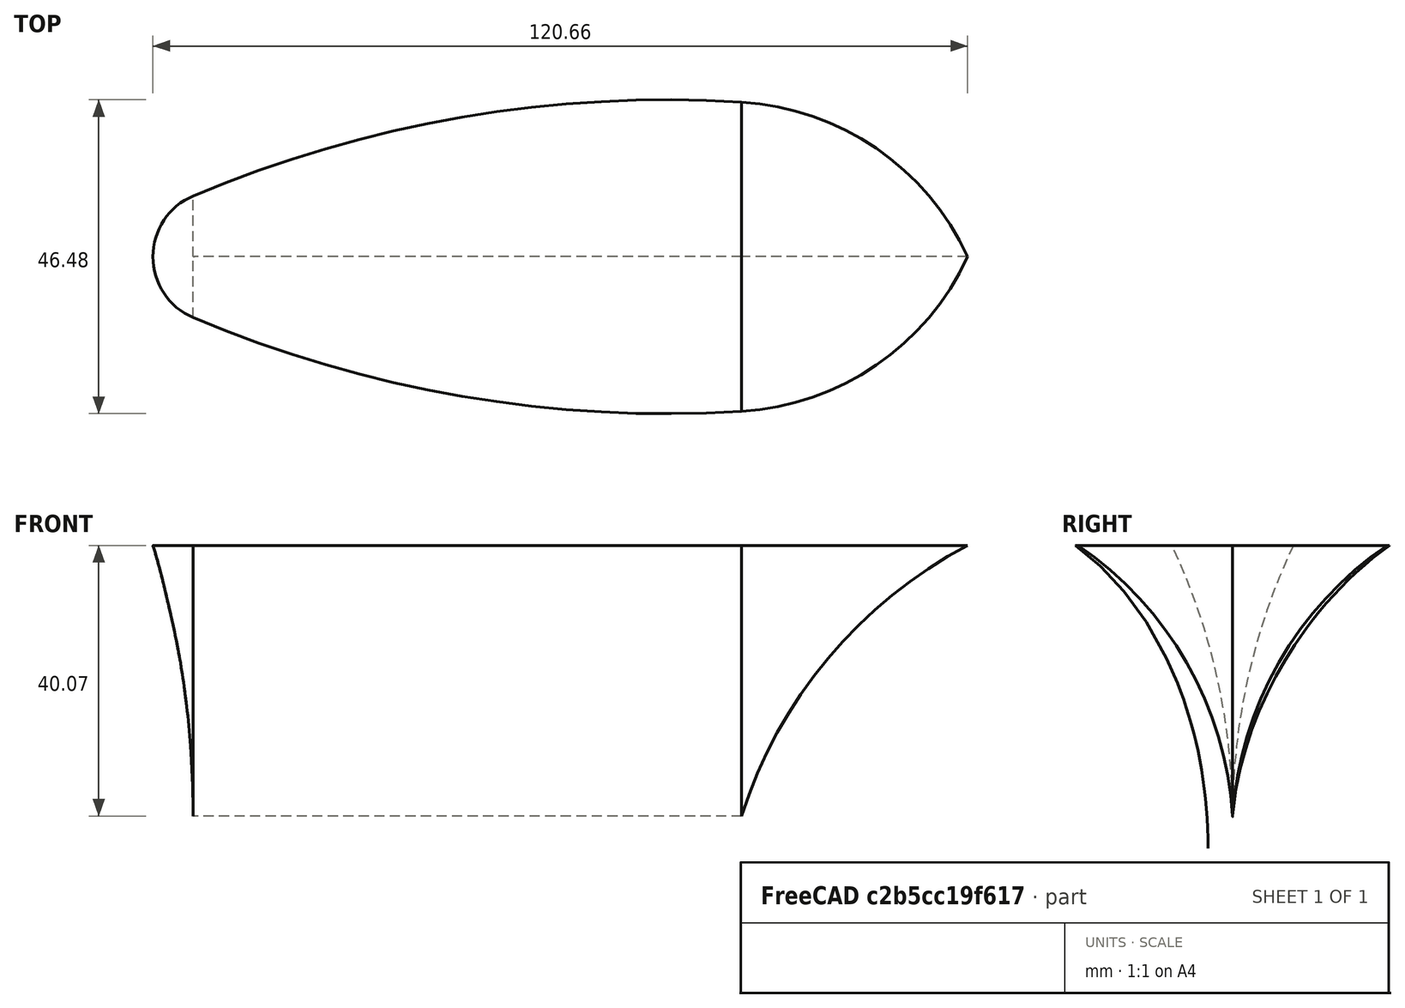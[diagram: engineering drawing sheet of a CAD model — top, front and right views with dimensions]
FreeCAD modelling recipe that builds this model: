
FCSTD DOCUMENT  (FreeCAD 0.21R33771 (Git))
Label: ship
License: All rights reserved
LicenseURL: http://en.wikipedia.org/wiki/All_rights_reserved
objects: Surface::Filling×6, Sketcher::SketchObject×5, Part::RuledSurface×1
note: 12 computed .brp shape members not serialized (recipe doc carries the construction recipe); baked Part::Feature solids carry a one-line shape summary decoded from their .brp

FEATURE [Sketcher::SketchObject] Sketch
  FullyConstrained = false
  sketch-geometry (7):
    g0: ArcOfCircle CenterX=-43.5861 CenterY=0 CenterZ=0 NormalX=0 NormalY=0 NormalZ=1 AngleXU=0 Radius=9.7712 StartAngle=1.97126 EndAngle=4.31193
    g1: ArcOfCircle CenterX=31.4054 CenterY=-16.5595 CenterZ=0 NormalX=0 NormalY=0 NormalZ=1 AngleXU=0 Radius=39.5318 StartAngle=0.432222 EndAngle=1.50927
    g2: ArcOfCircle CenterX=31.4054 CenterY=16.5595 CenterZ=0 NormalX=0 NormalY=0 NormalZ=1 AngleXU=0 Radius=39.5318 StartAngle=4.77392 EndAngle=5.85096
    g3: ArcOfCircle CenterX=22.7694 CenterY=-156.743 CenterZ=0 NormalX=0 NormalY=0 NormalZ=1 AngleXU=0 Radius=179.981 StartAngle=1.50927 EndAngle=1.97126
    g4: ArcOfCircle CenterX=22.7694 CenterY=156.743 CenterZ=0 NormalX=0 NormalY=0 NormalZ=1 AngleXU=0 Radius=179.981 StartAngle=4.31193 EndAngle=4.77392
    g5: LineSegment StartX=67.3018 StartY=-7.1e-15 StartZ=0 EndX=33.8361 EndY=0 EndZ=0
    g6: LineSegment StartX=-53.3573 StartY=0 StartZ=0 EndX=-47.3953 EndY=0 EndZ=0
  constraints (17):
    c: PointOnObject(g1,g-1)
    c: Coincident(g2,g1)
    c: Equal(g1,g2)
    c: Vertical(g1,g2)
    c: Tangent(g3,g0) = -1.5708
    c: Tangent(g4,g0) = -1.5708
    c: Tangent(g3,g1) = -1.5708
    c: Tangent(g4,g2) = -1.5708
    c: PointOnObject(g0,g-1)
    c: Vertical(g0,g0)
    c: Coincident(g5,g1)
    c: PointOnObject(g5,g-1)
    c: Vertical(g1,g5)
    c: PointOnObject(g6,g0)
    c: PointOnObject(g6,g-1)
    c: Horizontal(g6)
    c: Vertical(g0,g6)
FEATURE [Sketcher::SketchObject] Sketch001
  ExternalGeometry = -> [Sketch]
  FullyConstrained = false
  MapMode = 7
  Placement = pos=(33.8361,0,0) rot=(0.57735,0.57735,0.57735;2.0944rad)
  Support = -> [Sketch]
  sketch-geometry (2):
    g0: ArcOfCircle CenterX=-52.4068 CenterY=-43.4397 CenterZ=0 NormalX=0 NormalY=0 NormalZ=1 AngleXU=0 Radius=52.5148 StartAngle=0.0641414 EndAngle=0.974088
    g1: ArcOfCircle CenterX=52.4068 CenterY=-43.4397 CenterZ=0 NormalX=0 NormalY=0 NormalZ=1 AngleXU=0 Radius=52.5148 StartAngle=2.1675 EndAngle=3.07745
  constraints (4):
    c: Coincident(g0,g-4)
    c: Coincident(g1,g-3)
    c: Coincident(g1,g0)
    c: Symmetric(g0,g1,g-2)
FEATURE [Sketcher::SketchObject] Sketch002
  ExternalGeometry = -> [Sketch,Sketch001]
  FullyConstrained = false
  Placement = pos=(0,0,0) rot=(1,0,0;1.5708rad)
  sketch-geometry (2):
    g0: ArcOfCircle CenterX=99.3271 CenterY=-60.7549 CenterZ=0 NormalX=0 NormalY=0 NormalZ=1 AngleXU=0 Radius=68.6789 StartAngle=2.05591 EndAngle=2.83571
    g1: LineSegment StartX=33.8361 StartY=-40.0736 StartZ=0 EndX=-47.3953 EndY=-40.0736 EndZ=0
  constraints (5):
    c: Coincident(g0,g-3)
    c: Coincident(g0,g-4)
    c: Coincident(g1,g0)
    c: Horizontal(g1)
    c: Vertical(g-5,g1)
FEATURE [Sketcher::SketchObject] Sketch003
  ExternalGeometry = -> [Sketch002,Sketch]
  FullyConstrained = false
  MapMode = 7
  Placement = pos=(-47.3953,0,0) rot=(0.57735,-0.57735,-0.57735;2.0944rad)
  Support = -> [Sketch]
  sketch-geometry (2):
    g0: ArcOfCircle CenterX=93.7343 CenterY=-40.0736 CenterZ=0 NormalX=0 NormalY=0 NormalZ=1 AngleXU=0 Radius=93.7343 StartAngle=2.69984 EndAngle=3.14159
    g1: ArcOfCircle CenterX=-93.7344 CenterY=-40.0737 CenterZ=0 NormalX=0 NormalY=0 NormalZ=1 AngleXU=0 Radius=93.7344 StartAngle=3.42796e-07 EndAngle=0.441751
  constraints (4):
    c: Coincident(g0,g-3)
    c: Tangent(g0,g-2)
    c: Coincident(g1,g0)
    c: Tangent(g1,g-2)
FEATURE [Sketcher::SketchObject] Sketch004
  ExternalGeometry = -> [Sketch,Sketch003]
  FullyConstrained = true
  Placement = pos=(0,0,0) rot=(1,0,0;1.5708rad)
  sketch-geometry (1):
    g0: ArcOfCircle CenterX=-185.055 CenterY=-40.0736 CenterZ=0 NormalX=0 NormalY=0 NormalZ=1 AngleXU=0 Radius=137.66 StartAngle=6.28319 EndAngle=6.57857
  constraints (3):
    c: Coincident(g0,g-3)
    c: Coincident(g0,g-4)
    c: Tangent(g0,g-4)
FEATURE [Surface::Filling] Surface
  Anisotropy = false
  BoundaryEdges = -> [Sketch001,Sketch002,Sketch]
  BoundaryOrder = [0,0,0]
  Degree = 3
  Iterations = 2
  MaximumDegree = 8
  MaximumSegments = 9
  PointsOnCurve = 15
  TolAngular = 0.01
  TolCurvature = 0.1
  Tolerance2d = 1e-05
  Tolerance3d = 0.0001
FEATURE [Surface::Filling] Surface001
  Anisotropy = false
  BoundaryEdges = -> [Sketch002,Sketch001,Sketch]
  BoundaryOrder = [0,0,0]
  Degree = 3
  Iterations = 2
  MaximumDegree = 8
  MaximumSegments = 9
  PointsOnCurve = 15
  TolAngular = 0.01
  TolCurvature = 0.1
  Tolerance2d = 1e-05
  Tolerance3d = 0.0001
FEATURE [Surface::Filling] Surface002
  Anisotropy = false
  BoundaryEdges = -> [Sketch003,Sketch004,Sketch]
  BoundaryOrder = [0,0,0,0]
  Degree = 3
  Iterations = 2
  MaximumDegree = 8
  MaximumSegments = 9
  PointsOnCurve = 15
  TolAngular = 0.01
  TolCurvature = 0.1
  Tolerance2d = 1e-05
  Tolerance3d = 0.0001
FEATURE [Surface::Filling] Surface003
  Anisotropy = false
  BoundaryEdges = -> [Surface002,Sketch,Surface]
  BoundaryOrder = [0,0,0]
  Degree = 3
  Iterations = 2
  MaximumDegree = 8
  MaximumSegments = 9
  PointsOnCurve = 15
  TolAngular = 0.01
  TolCurvature = 0.1
  Tolerance2d = 1e-05
  Tolerance3d = 0.0001
FEATURE [Surface::Filling] Surface004
  Anisotropy = false
  BoundaryEdges = -> [Sketch]
  BoundaryOrder = [0,0,0,0,0]
  Degree = 3
  Iterations = 2
  MaximumDegree = 8
  MaximumSegments = 9
  PointsOnCurve = 15
  TolAngular = 0.01
  TolCurvature = 0.1
  Tolerance2d = 1e-05
  Tolerance3d = 0.0001
FEATURE [Surface::Filling] Surface005
  Anisotropy = false
  BoundaryEdges = -> [Sketch003,Sketch,Sketch002,Sketch001]
  BoundaryOrder = [0,0,0,0]
  Degree = 3
  Iterations = 2
  MaximumDegree = 8
  MaximumSegments = 9
  PointsOnCurve = 15
  TolAngular = 0.01
  TolCurvature = 0.1
  Tolerance2d = 1e-05
  Tolerance3d = 0.0001
FEATURE [Part::RuledSurface] Ruled_Surface
  Curve1 = -> Surface [Edge1]
  Curve2 = -> Sketch001 [Edge1]
  Orientation = 0
